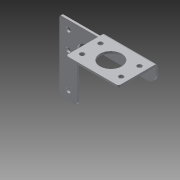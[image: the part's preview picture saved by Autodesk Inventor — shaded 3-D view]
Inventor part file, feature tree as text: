
AUTODESK INVENTOR PART (.ipt)
format: ipt  version: 2013 (Build 170138000, 138)  size: 159,744 bytes
history: native  units: in
note: dims shown in document units (in); Inventor stores cm internally (conversion verified against a paired STEP export)
features: sheet_metal_op x4, sketch x3, other x3, chamfer x1
ambient origin geometry x8: Origin, YZ Plane, XZ Plane, XY Plane, X Axis, Y Axis, Z Axis, Center Point
bodies: Solid1 (feature_tree)
feature tree (11):
  sheet_metal_op  "Face1"
  sheet_metal_op  "Flange1"
  chamfer  "Corner Round1"
  sketch  "Sketch1"  dims[d0=1.0in]
  other  "Plate1"
  sketch  "Sketch2"  dims[d2=0.26in]
  other  "Plate2"
  sheet_metal_op  "Bend1"
  sheet_metal_op  "Corner1"
  sketch  "Sketch3"  dims[d3=0.26in d4=2.0in d5=1.0in d6=4.5in d7=0.75in d8=3.0in d9=0.125in d10=0.12in d11=0.12in d12=0.06in d13=0.24in d14=0.12in d15=2.25in d16=90.0deg d17=0.05in d18=0.48in d19=0.12in d20=0.12in d21=0.5in d22=0.125in d23=0.26in d25=0.375in d26=0.5in d27=0.12in d28=0.0in d29=0.53in d30=0.395in d31=1.25in d32=2.0in d33=0.26in d34=0.5in]
  other  "Cut1"
